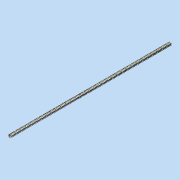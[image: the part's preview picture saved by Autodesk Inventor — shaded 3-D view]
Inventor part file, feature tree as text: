
AUTODESK INVENTOR PART (.ipt)
format: ipt  version: 2015 (Build 190159000, 159)  size: 1,124,352 bytes
history: native  units: in
note: dims shown in document units (in); Inventor stores cm internally (conversion verified against a paired STEP export)
features: sketch x5, helix x4, extrude x1, other x1
ambient origin geometry x8: Origin, YZ Plane, XZ Plane, XY Plane, X Axis, Y Axis, Z Axis, Center Point
bodies: Solid1 (feature_tree)
feature tree (11):
  extrude  "Extrusion1"  Depth=15.9449in TaperAngle=0.0deg
  helix  "Coil2"  [1 undecoded]
  helix  "Coil6"  [1 undecoded]
  helix  "Coil7"  [1 undecoded]
  helix  "Coil8"  [1 undecoded]
  other  "Move Face1"
  sketch  "Sketch1"  dims[d0=0.315in d1=15.9449in d2=0.0in d3=0.1993in d4=0.0996in d5=0.0in d6=0.7181in]
  sketch  "Sketch2"  dims[d9=0.0411in]
  sketch  "Sketch9"  dims[d10=0.0725in]
  sketch  "Sketch10"  dims[d20=0.5in d21=1.0in d22=19.685in d23=0.0in d24=90.0deg d25=90.0deg d26=0.0in d27=0.0in]
  sketch  "Sketch11"  dims[d91=15.0deg d92=30.0deg d93=0.0411in d94=0.125in d95=0.0725in d96=0.5in d97=1.0in d98=19.685in d99=0.0in d100=90.0deg d101=90.0deg d102=0.0in d103=0.0in d105=30.0deg d107=0.0725in d108=0.0411in d109=0.5in d110=1.0in d111=19.685in d112=0.0in d113=90.0deg d114=90.0deg d115=0.0in d116=0.0in d118=30.0deg d119=0.0725in d120=0.0411in d122=0.5in d123=1.0in d124=19.685in d125=0.0in d126=90.0deg d127=90.0deg d128=0.0in d129=0.0in]
note: 4 required parameter values undecoded (feature->parameter linkage not recoverable at this tier; creation-order binding heuristic only, values carry confidence <= 0.55)
